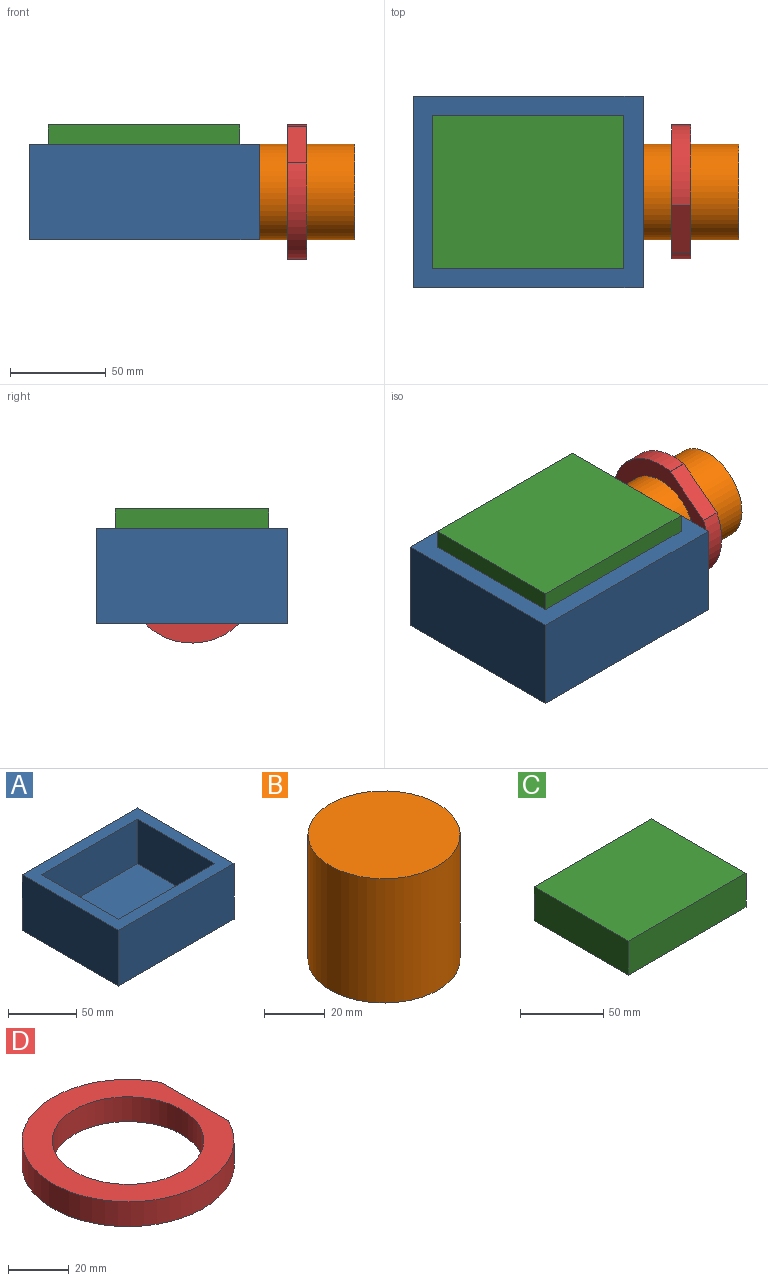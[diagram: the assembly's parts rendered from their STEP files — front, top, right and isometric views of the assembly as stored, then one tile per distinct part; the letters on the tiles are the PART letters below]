
ASSEMBLY  parts=4 mates=3
PART A: 11 faces, bbox 120x100x50 mm
  f0: plane 120x100mm, normal (0,0,1), area 4000mm2, adj f1,f2,f3,f4,f6,f7,f8,f9
  f1: plane 120x50mm, normal (0,1,0), area 6000mm2, adj f0,f2,f4,f5
  f2: plane 100x50mm, normal (-1,0,0), area 5000mm2, adj f0,f1,f3,f5
  f3: plane 120x50mm, normal (0,-1,0), area 6000mm2, adj f0,f2,f4,f5
  f4: plane 100x50mm, normal (1,0,0), area 5000mm2, adj f0,f1,f3,f5
  f5: plane 120x100mm, normal (0,0,-1), area 12000mm2, adj f1,f2,f3,f4
  f6: plane 100x40mm, normal (0,-1,0), area 4000mm2, adj f0,f7,f9,f10
  f7: plane 80x40mm, normal (1,0,0), area 3200mm2, adj f0,f6,f8,f10
  f8: plane 100x40mm, normal (0,1,0), area 4000mm2, adj f0,f7,f9,f10
  f9: plane 80x40mm, normal (-1,0,0), area 3200mm2, adj f0,f6,f8,f10
  f10: plane 100x80mm, normal (0,0,1), area 8000mm2, adj f6,f7,f8,f9
PART B: 3 faces, bbox 50x50x50 mm
  f0: cylinder r=25mm len=50mm, axis (0,0,-1), area 7854mm2, adj f1,f2
  f1: plane 50x50mm, normal (0,0,1), area 1963.5mm2, adj f0
  f2: plane 50x50mm, normal (0,0,-1), area 1963.5mm2, adj f0
PART C: 6 faces, bbox 100x80x25 mm
  f0: plane 100x25mm, normal (0,1,0), area 2500mm2, adj f1,f3,f4,f5
  f1: plane 80x25mm, normal (-1,0,0), area 2000mm2, adj f0,f2,f4,f5
  f2: plane 100x25mm, normal (0,-1,0), area 2500mm2, adj f1,f3,f4,f5
  f3: plane 80x25mm, normal (1,0,0), area 2000mm2, adj f0,f2,f4,f5
  f4: plane 100x80mm, normal (0,0,1), area 8000mm2, adj f0,f1,f2,f3
  f5: plane 100x80mm, normal (0,0,-1), area 8000mm2, adj f0,f1,f2,f3
PART D: 6 faces, bbox 66.4x70x10 mm
  f0: cylinder r=35mm len=70mm, axis (0,0,-1), area 1878mm2, adj f1,f2,f4,f5
  f1: plane 70x66.42mm, normal (0,0,1), area 1808.1mm2, adj f0,f3,f4,f5
  f2: plane 70x66.42mm, normal (0,0,-1), area 1808.1mm2, adj f0,f3,f4,f5
  f3: cylinder r=25mm len=50mm, axis (0,0,1), area 1570.8mm2, adj f1,f2
  f4: plane 10x0.08mm, normal (0,1,0), area 0.8mm2, adj f0,f1,f2,f5
  f5: plane 31x10mm, normal (1,0,0), area 310mm2, adj f0,f1,f2,f4
PLACE A at identity fixed
PLACE B rot(axis=(0,-1,0),90deg) t=(145,0,25)mm
PLACE C t=(0,0,25)mm
PLACE D rot(axis=(-0.69,0.24,-0.69),153.5deg) t=(-10,0,25)mm
MATE slider C.f4 <-> A.f0  axis (0,0,1) through (-50,40,60)mm
MATE revolute D.f3 <-> B.f0  axis (1,0,0) through (85,0,25)mm
MATE fastened B.f0 <-> A.f4  axis (1,0,0) through (60,0,25)mm
